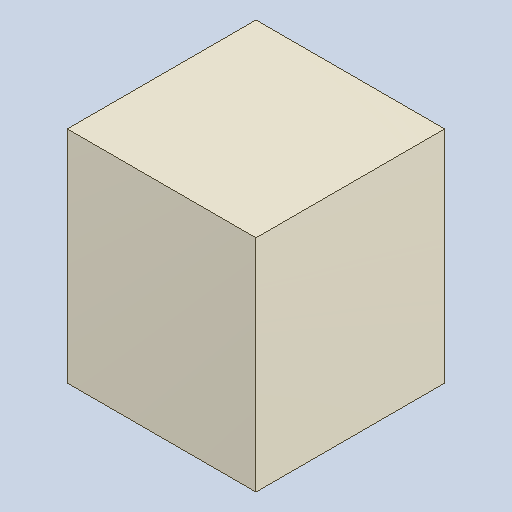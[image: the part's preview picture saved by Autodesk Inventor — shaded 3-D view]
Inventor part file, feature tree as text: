
AUTODESK INVENTOR PART (.ipt)
format: ipt  version: 2023.4 (Build 274418000, 418)  size: 82,944 bytes
history: native  units: mm
features: extrude x1
ambient origin geometry x8: Origin, YZ Plane, XZ Plane, XY Plane, X Axis, Y Axis, Z Axis, Center Point
bodies: Solid1 (feature_tree)
feature tree (1):
  extrude  "Extruded_13"  [1 undecoded]
note: 1 required parameter value undecoded (feature->parameter linkage not recoverable at this tier; creation-order binding heuristic only, values carry confidence <= 0.55)
